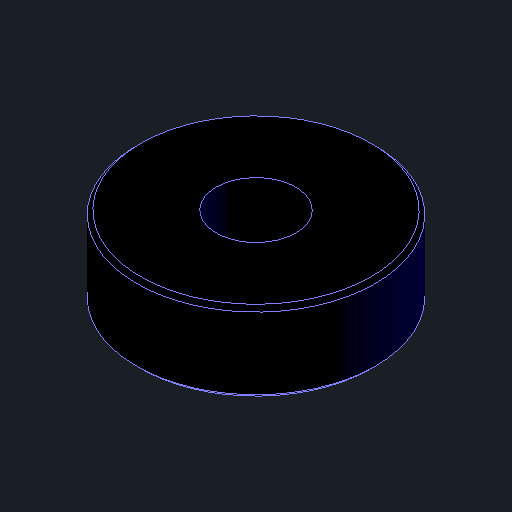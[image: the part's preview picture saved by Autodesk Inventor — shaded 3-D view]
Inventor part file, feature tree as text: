
AUTODESK INVENTOR PART (.ipt)
format: ipt  version: 2024 (Build 280153000, 153)  size: 108,544 bytes
history: native  units: mm
features: other x1, extrude x1, chamfer x1, sketch x1
ambient origin geometry x8: Origin, YZ Plane, XZ Plane, XY Plane, X Axis, Y Axis, Z Axis, Center Point
bodies: Body1 (feature_tree)
feature tree (4):
  other  "Твердое тело1"
  extrude  "Выдавливание1"  Depth=12.0mm
  chamfer  "Фаска1"  Distance=4.0mm
  sketch  "Эскиз1"
